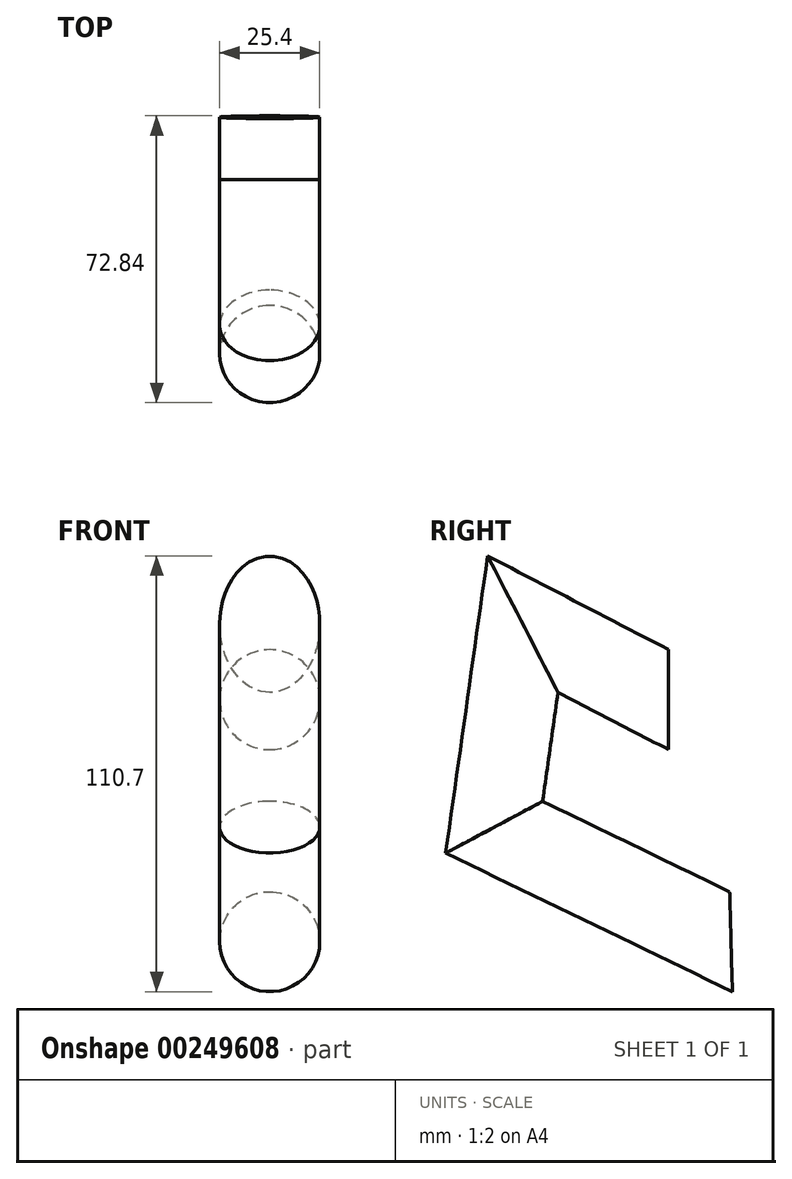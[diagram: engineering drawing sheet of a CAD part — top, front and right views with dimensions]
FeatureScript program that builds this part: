
annotation { "Feature Type Name" : "Feature", "Feature Type Description" : "" }
export const myFeature = defineFeature(function(context is Context, id is Id, definition is map)
    precondition{}
    {
        {
            var Q0;
            Q0=qCreatedBy(makeId("Front.planeOp"),FACE);
            var sketch = newSketch(context, id + "F0", { "sketchPlane" : qUnion([Q0])});
            skCircle(sketch, "E0", {"center": v(0, 0) * mm, "radius": 12.7 * mm});
            skSolve(sketch);
        }
        {
            var Q0;
            Q0=qCreatedBy(makeId("Right.planeOp"),FACE);
            var sketch = newSketch(context, id + "F1", { "sketchPlane" : qUnion([Q0])});
            skLineSegment(sketch, "E1", {"start": v(0, 0) * mm, "end": v(-37.03, 19.18) * mm});
            skLineSegment(sketch, "E2", {"start": v(-37.03, 19.18) * mm, "end": v(-44.3, -32.4) * mm});
            skLineSegment(sketch, "E3", {"start": v(-44.3, -32.4) * mm, "end": v(15.87, -61.5) * mm});
            skSolve(sketch);
        }
        {
            var Q0;
            Q0=makeQuery(id+"F0.imprint","IMPRINT",FACE,{"disambiguationData":[TD([[makeQuery(id+"F0.imprint","IMPRINT",EDGE,{"derivedFrom":sQuery(id+"F0.wireOp",EDGE,"E0")}),1.0]])]});
            var Q1;
            Q1=sQuery(id+"F1.wireOp",EDGE,"E3");
            var Q2;
            Q2=sQuery(id+"F1.wireOp",EDGE,"E2");
            var Q3;
            Q3=sQuery(id+"F1.wireOp",EDGE,"E1");
            sweep(context, id + "F2", {"profiles" : qUnion([Q0]), "path" : qUnion([Q1, Q2, Q3])});
        }
    });
